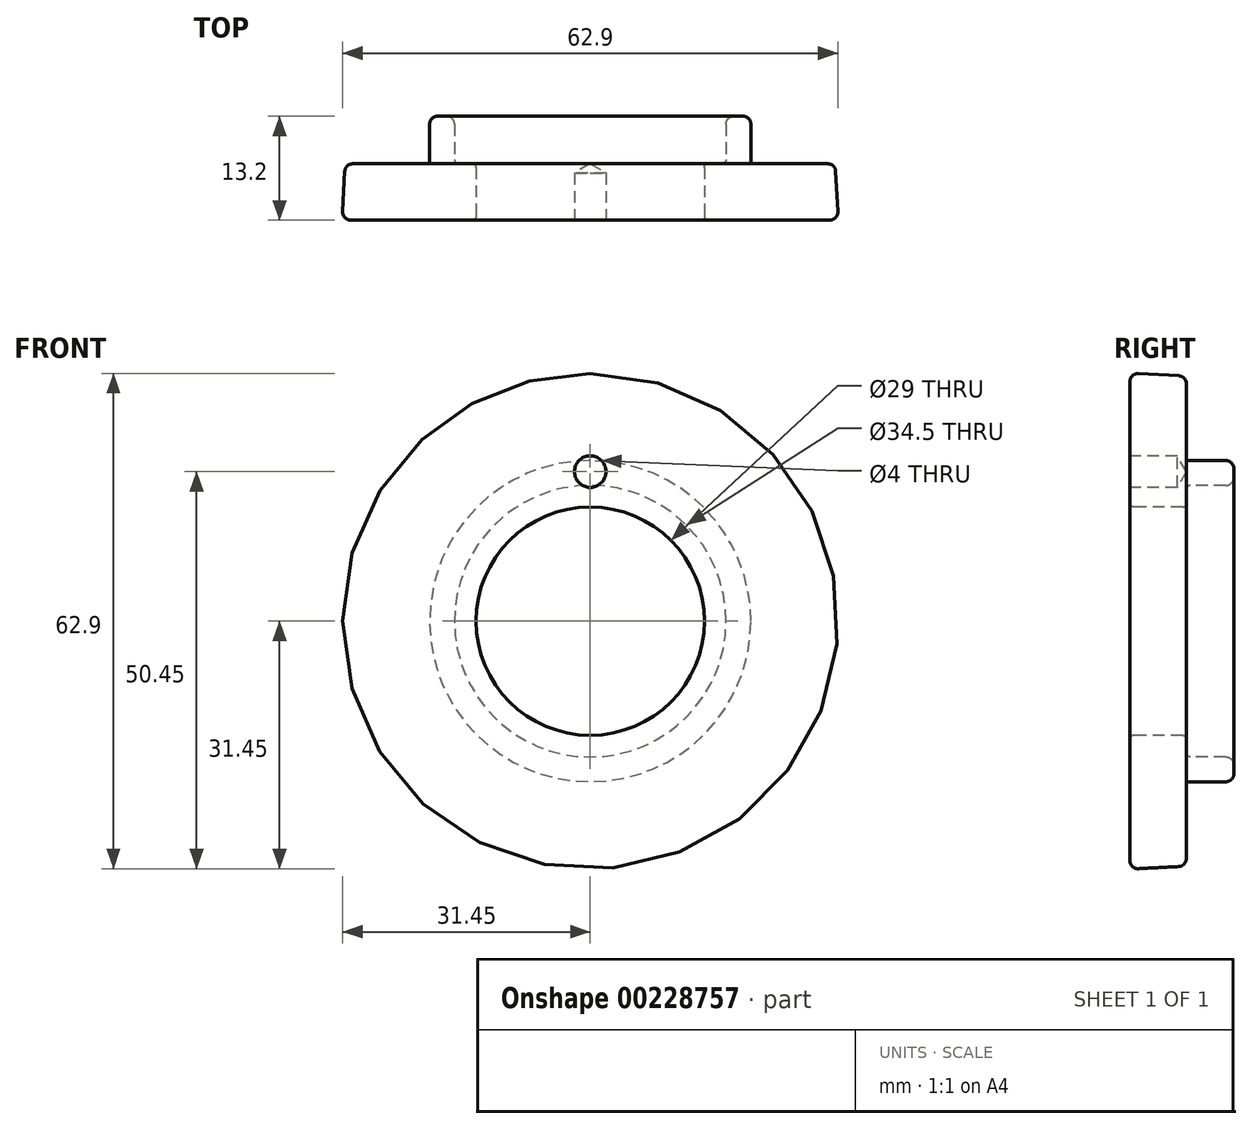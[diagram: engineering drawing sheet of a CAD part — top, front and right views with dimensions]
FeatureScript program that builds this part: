
annotation { "Feature Type Name" : "Feature", "Feature Type Description" : "" }
export const myFeature = defineFeature(function(context is Context, id is Id, definition is map)
    precondition{}
    {
        {
            var Q0;
            Q0=qCreatedBy(makeId("Right.planeOp"),FACE);
            var sketch = newSketch(context, id + "F0", { "sketchPlane" : qUnion([Q0])});
            skLineSegment(sketch, "E0", {"start": v(0, 14.5) * mm, "end": v(7.2, 14.5) * mm});
            skLineSegment(sketch, "E1", {"start": v(7.2, 14.5) * mm, "end": v(7.2, 17.25) * mm});
            skLineSegment(sketch, "E2", {"start": v(7.2, 17.25) * mm, "end": v(13.2, 17.25) * mm});
            skLineSegment(sketch, "E3", {"start": v(13.2, 17.25) * mm, "end": v(13.2, 20.4) * mm});
            skLineSegment(sketch, "E4", {"start": v(13.2, 20.4) * mm, "end": v(7.16, 20.4) * mm});
            skLineSegment(sketch, "E5", {"start": v(7.16, 20.4) * mm, "end": v(7.16, 31.12) * mm});
            skLineSegment(sketch, "E6", {"start": v(0, 31.5) * mm, "end": v(0, 14.5) * mm});
            skLineSegment(sketch, "E7", {"start": v(0, 31.5) * mm, "end": v(7.16, 31.12) * mm});
            skLineSegment(sketch, "E8", {"start": v(0, 0) * mm, "end": v(8.32, 0) * mm});
            skSolve(sketch);
        }
        {
            var Q0;
            Q0=makeQuery(id+"F0.imprint","IMPRINT",FACE,{"disambiguationData":[TD([[makeQuery(id+"F0.imprint","IMPRINT",EDGE,{"derivedFrom":sQuery(id+"F0.wireOp",EDGE,"E0")}),1.0]])]});
            var Q1;
            Q1=sQuery(id+"F0.wireOp",EDGE,"E8");
            revolve(context, id + "F1", {"entities" : qUnion([Q0]), "axis" : qUnion([Q1]), "revolveType" : RevolveType.FULL});
        }
        {
            var Q0;
            Q0=makeQuery(id+"F1.opRevolve","SWEPT_FACE",FACE,{"disambiguationData":[OSD([sQuery(id+"F0.wireOp",EDGE,"E6")])]});
            var sketch = newSketch(context, id + "F2", { "sketchPlane" : qUnion([Q0])});
            skCircle(sketch, "E9", {"center": v(0, 0) * mm, "radius": 19 * mm, "construction": true});
            skPoint(sketch, "E10", {"position": v(0, 19) * mm});
            skSolve(sketch);
        }
        {
            var Q0;
            Q0=sQuery(id+"F2.wireOp",VERTEX,"E10");
            var Q1;
            Q1=makeQuery(id+"F1.opRevolve","SWEPT_BODY",BODY,{"disambiguationData":[OSD([sQuery(id+"F0.wireOp",EDGE,"E0"),sQuery(id+"F0.wireOp",EDGE,"E1"),sQuery(id+"F0.wireOp",EDGE,"E2"),sQuery(id+"F0.wireOp",EDGE,"E3"),sQuery(id+"F0.wireOp",EDGE,"E4"),sQuery(id+"F0.wireOp",EDGE,"E5"),sQuery(id+"F0.wireOp",EDGE,"E6"),sQuery(id+"F0.wireOp",EDGE,"E7")])]});
            hole(context, id + "F3", {"style" : HoleStyle.SIMPLE, "endStyle" : HoleEndStyle.BLIND, "holeDiameter" : 4 * mm, "holeDepth" : 6 * mm, "startFromSketch" : true, "locations" : qUnion([Q0]), "scope" : qUnion([Q1])});
        }
        {
            var Q0;
            Q0=makeQuery(id+"F1.opRevolve","SWEPT_EDGE",EDGE,{"disambiguationData":[OSD([sQuery(id+"F0.wireOp",EDGE,"E6"),sQuery(id+"F0.wireOp",EDGE,"E7")])]});
            var Q1;
            Q1=makeQuery(id+"F1.opRevolve","SWEPT_EDGE",EDGE,{"disambiguationData":[OSD([sQuery(id+"F0.wireOp",EDGE,"E5"),sQuery(id+"F0.wireOp",EDGE,"E7")])]});
            var Q2;
            Q2=makeQuery(id+"F1.opRevolve","SWEPT_EDGE",EDGE,{"disambiguationData":[OSD([sQuery(id+"F0.wireOp",EDGE,"E3"),sQuery(id+"F0.wireOp",EDGE,"E4")])]});
            fillet(context, id + "F4", {"entities" : qUnion([Q0, Q1, Q2]), "radius" : 1 * mm, "tangentPropagation" : true, "allowEdgeOverflow" : false});
        }
        {
            var Q0;
            Q0=makeQuery(id+"F1.opRevolve","SWEPT_EDGE",EDGE,{"disambiguationData":[OSD([sQuery(id+"F0.wireOp",EDGE,"E0"),sQuery(id+"F0.wireOp",EDGE,"E6")])]});
            var Q1;
            Q1=makeQuery(id+"F1.opRevolve","SWEPT_EDGE",EDGE,{"disambiguationData":[OSD([sQuery(id+"F0.wireOp",EDGE,"E0"),sQuery(id+"F0.wireOp",EDGE,"E1")])]});
            var Q2;
            Q2=makeQuery(id+"F1.opRevolve","SWEPT_EDGE",EDGE,{"disambiguationData":[OSD([sQuery(id+"F0.wireOp",EDGE,"E1"),sQuery(id+"F0.wireOp",EDGE,"E2")])]});
            fillet(context, id + "F5", {"entities" : qUnion([Q0, Q1, Q2]), "radius" : 0.5 * mm, "tangentPropagation" : true, "allowEdgeOverflow" : false});
        }
        {
            var Q0;
            Q0=makeQuery(id+"F1.opRevolve","SWEPT_EDGE",EDGE,{"disambiguationData":[OSD([sQuery(id+"F0.wireOp",EDGE,"E2"),sQuery(id+"F0.wireOp",EDGE,"E3")])]});
            fillet(context, id + "F6", {"entities" : qUnion([Q0]), "radius" : 1 * mm, "tangentPropagation" : true, "allowEdgeOverflow" : false});
        }
    });
